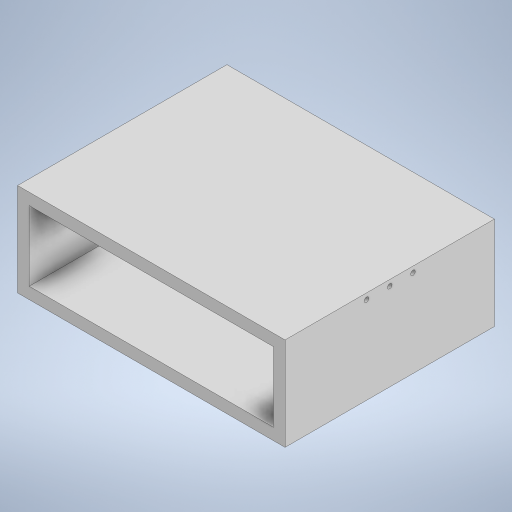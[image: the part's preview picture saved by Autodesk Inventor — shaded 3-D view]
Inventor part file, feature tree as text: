
AUTODESK INVENTOR PART (.ipt)
format: ipt  version: 2024 (Build 280153000, 153)  size: 211,968 bytes
history: native  units: in
note: dims shown in document units (in); Inventor stores cm internally (conversion verified against a paired STEP export)
features: other x4, extrude x2, hole x2
ambient origin geometry x8: Origin, YZ Plane, XZ Plane, XY Plane, X Axis, Y Axis, Z Axis, Center Point
bodies: Solid1 (feature_tree)
feature tree (8):
  extrude  "BottomBoxWidth"  Depth=4.0in
  extrude  "TrayCut"  Depth=11.5in
  hole  "RightPlateHoles"  [1 undecoded]
  hole  "LeftPlateHoles"  [1 undecoded]
  other  "BottomBoxFrame"
  other  "TrayShape"
  other  "RightHoleGeo"
  other  "LeftHoleGeo"
note: 2 required parameter values undecoded (feature->parameter linkage not recoverable at this tier; creation-order binding heuristic only, values carry confidence <= 0.55)
